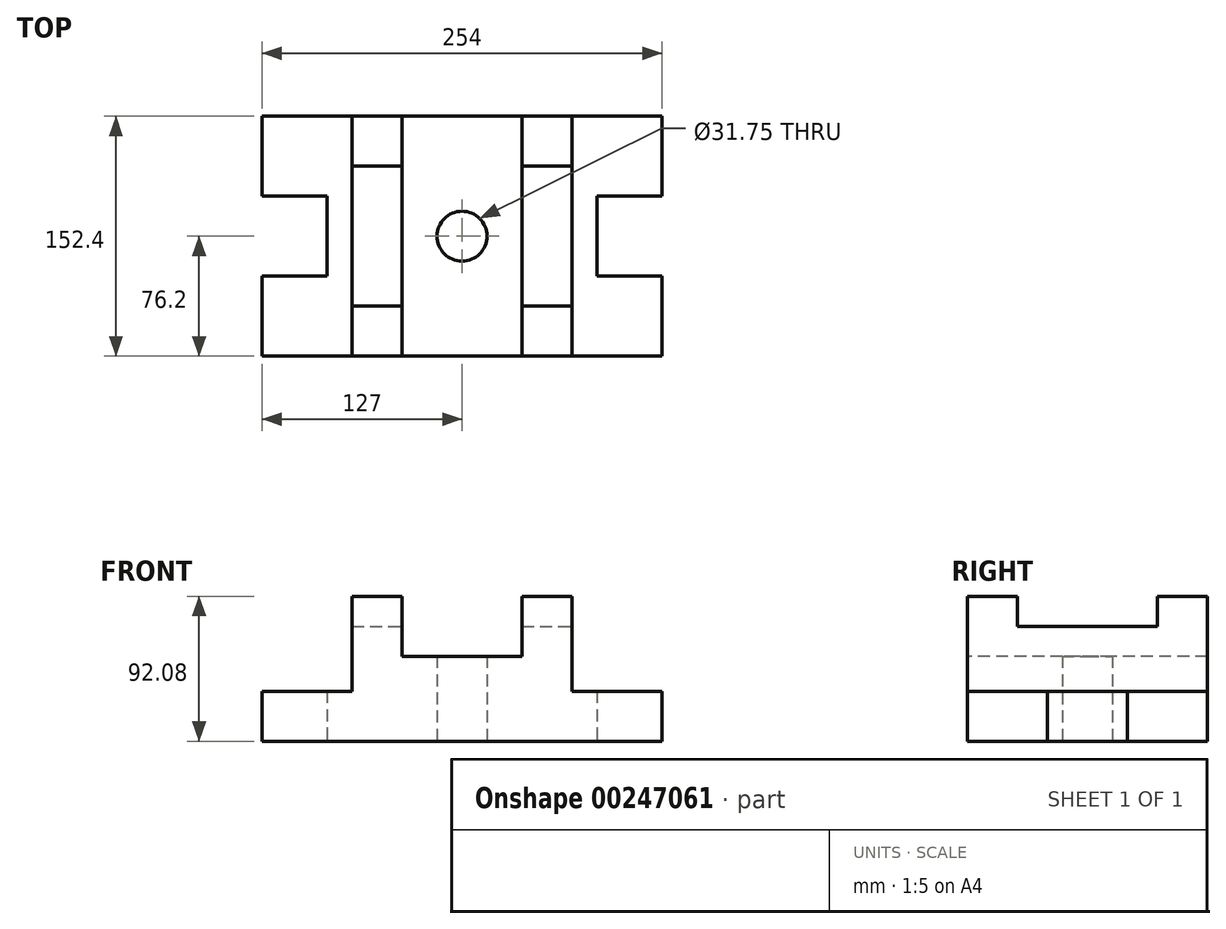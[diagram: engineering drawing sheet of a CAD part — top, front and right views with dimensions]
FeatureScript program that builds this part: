
annotation { "Feature Type Name" : "Feature", "Feature Type Description" : "" }
export const myFeature = defineFeature(function(context is Context, id is Id, definition is map)
    precondition{}
    {
        {
            var Q0;
            Q0=qCreatedBy(makeId("Top.planeOp"),FACE);
            var sketch = newSketch(context, id + "F0", { "sketchPlane" : qUnion([Q0])});
            skLineSegment(sketch, "E0.bottom", {"start": v(127, -76.2) * mm, "end": v(-127, -76.2) * mm});
            skLineSegment(sketch, "E0.top", {"start": v(127, 76.2) * mm, "end": v(-127, 76.2) * mm});
            skLineSegment(sketch, "E0.left", {"start": v(127, -76.2) * mm, "end": v(127, -25.4) * mm});
            skLineSegment(sketch, "E0.right", {"start": v(-127, -76.2) * mm, "end": v(-127, -25.4) * mm});
            skPoint(sketch, "E0.middle", {"position": v(0, 0) * mm});
            skLineSegment(sketch, "E1", {"start": v(38.1, 76.2) * mm, "end": v(38.1, -76.2) * mm});
            skLineSegment(sketch, "E2", {"start": v(-38.1, 76.2) * mm, "end": v(-38.1, -76.2) * mm});
            skLineSegment(sketch, "E3", {"start": v(69.85, 76.2) * mm, "end": v(69.85, -76.2) * mm});
            skLineSegment(sketch, "E4", {"start": v(-69.85, 76.2) * mm, "end": v(-69.85, -76.2) * mm});
            skLineSegment(sketch, "E5", {"start": v(-69.85, -44.45) * mm, "end": v(-38.1, -44.45) * mm});
            skLineSegment(sketch, "E6", {"start": v(-69.85, 44.45) * mm, "end": v(-38.1, 44.45) * mm});
            skLineSegment(sketch, "E7", {"start": v(38.1, 44.45) * mm, "end": v(69.85, 44.45) * mm});
            skLineSegment(sketch, "E8", {"start": v(38.1, -44.45) * mm, "end": v(69.85, -44.45) * mm});
            skLineSegment(sketch, "E9", {"start": v(-85.72, 25.4) * mm, "end": v(-85.72, -25.4) * mm});
            skLineSegment(sketch, "E10", {"start": v(85.72, 25.4) * mm, "end": v(85.72, -25.4) * mm});
            skLineSegment(sketch, "E11", {"start": v(85.72, -25.4) * mm, "end": v(127, -25.4) * mm});
            skLineSegment(sketch, "E12", {"start": v(85.72, 25.4) * mm, "end": v(127, 25.4) * mm});
            skLineSegment(sketch, "E13.trimOffspring", {"start": v(127, 25.4) * mm, "end": v(127, 76.2) * mm});
            skLineSegment(sketch, "E14", {"start": v(-127, 25.4) * mm, "end": v(-85.72, 25.4) * mm});
            skLineSegment(sketch, "E15", {"start": v(-127, -25.4) * mm, "end": v(-85.72, -25.4) * mm});
            skLineSegment(sketch, "E16.trimOffspring", {"start": v(-127, 25.4) * mm, "end": v(-127, 76.2) * mm});
            skCircle(sketch, "E17", {"center": v(0, 0) * mm, "radius": 15.88 * mm});
            skPoint(sketch, "E18.trimOffspring.end.orphan", {"position": v(0, -76.2) * mm});
            skPoint(sketch, "E19.start.orphan", {"position": v(0, 76.2) * mm});
            skSolve(sketch);
        }
        {
            var Q0;
            {var subQ0=sQuery(id+"F0.wireOp",EDGE,"E0.left");Q0=makeQuery(id+"F0.imprint","IMPRINT",FACE,{"disambiguationData":[TD([[makeQuery(id+"F0.imprint","IMPRINT",EDGE,{"derivedFrom":subQ0}),1.0]])]});}
            var Q1;
            {var subQ4=sQuery(id+"F0.wireOp",EDGE,"E12");Q1=makeQuery(id+"F0.imprint","IMPRINT",FACE,{"disambiguationData":[TD([[makeQuery(id+"F0.imprint","IMPRINT",EDGE,{"derivedFrom":subQ4}),1.0]])]});}
            var Q2;
            {var subQ4=sQuery(id+"F0.wireOp",EDGE,"E14");Q2=makeQuery(id+"F0.imprint","IMPRINT",FACE,{"disambiguationData":[TD([[makeQuery(id+"F0.imprint","IMPRINT",EDGE,{"derivedFrom":subQ4}),1.0]])]});}
            var Q3;
            {var subQ0=sQuery(id+"F0.wireOp",EDGE,"E0.right");Q3=makeQuery(id+"F0.imprint","IMPRINT",FACE,{"disambiguationData":[TD([[makeQuery(id+"F0.imprint","IMPRINT",EDGE,{"derivedFrom":subQ0}),-1.0]])]});}
            var Q4;
            {var subQ0=sQuery(id+"F0.wireOp",EDGE,"E4");var subQ7=sQuery(id+"F0.wireOp",EDGE,"E0.bottom");var subQ8=makeQuery(id+"F0.imprint","INTERSECT",VERTEX,{"derivedFrom":[subQ7,subQ0]});Q4=makeQuery(id+"F0.imprint","IMPRINT",FACE,{"disambiguationData":[TD([[makeQuery(id+"F0.imprint","IMPRINT",EDGE,{"disambiguationData":[TD([[subQ8,-1.0]])],"derivedFrom":subQ7}),-1.0]])]});}
            var Q5;
            {var subQ0=sQuery(id+"F0.wireOp",EDGE,"E3");var subQ9=sQuery(id+"F0.wireOp",EDGE,"E0.bottom");var subQ11=makeQuery(id+"F0.imprint","INTERSECT",VERTEX,{"derivedFrom":[subQ9,subQ0]});Q5=makeQuery(id+"F0.imprint","IMPRINT",FACE,{"disambiguationData":[TD([[makeQuery(id+"F0.imprint","IMPRINT",EDGE,{"disambiguationData":[TD([[subQ11,1.0]])],"derivedFrom":subQ9}),-1.0]])]});}
            extrude(context, id + "F1", {"entities" : qUnion([Q0, Q1, Q2, Q3, Q4, Q5]), "depth" : 31.75 * mm});
        }
        {
            var Q0;
            {var subQ0=sQuery(id+"F0.wireOp",EDGE,"E5");Q0=makeQuery(id+"F0.imprint","IMPRINT",FACE,{"disambiguationData":[TD([[makeQuery(id+"F0.imprint","IMPRINT",EDGE,{"derivedFrom":subQ0}),1.0]])]});}
            var Q1;
            {var subQ0=sQuery(id+"F0.wireOp",EDGE,"E7");Q1=makeQuery(id+"F0.imprint","IMPRINT",FACE,{"disambiguationData":[TD([[makeQuery(id+"F0.imprint","IMPRINT",EDGE,{"derivedFrom":subQ0}),-1.0]])]});}
            extrude(context, id + "F2", {"entities" : qUnion([Q0, Q1]), "operationType" : NewBodyOperationType.ADD, "depth" : 73.02 * mm});
        }
        {
            var Q0;
            {var subQ5=sQuery(id+"F0.wireOp",EDGE,"E8");Q0=makeQuery(id+"F0.imprint","IMPRINT",FACE,{"disambiguationData":[TD([[makeQuery(id+"F0.imprint","IMPRINT",EDGE,{"derivedFrom":subQ5}),-1.0]])]});}
            var Q1;
            {var subQ5=sQuery(id+"F0.wireOp",EDGE,"E5");Q1=makeQuery(id+"F0.imprint","IMPRINT",FACE,{"disambiguationData":[TD([[makeQuery(id+"F0.imprint","IMPRINT",EDGE,{"derivedFrom":subQ5}),-1.0]])]});}
            var Q2;
            {var subQ5=sQuery(id+"F0.wireOp",EDGE,"E6");Q2=makeQuery(id+"F0.imprint","IMPRINT",FACE,{"disambiguationData":[TD([[makeQuery(id+"F0.imprint","IMPRINT",EDGE,{"derivedFrom":subQ5}),1.0]])]});}
            var Q3;
            {var subQ5=sQuery(id+"F0.wireOp",EDGE,"E7");Q3=makeQuery(id+"F0.imprint","IMPRINT",FACE,{"disambiguationData":[TD([[makeQuery(id+"F0.imprint","IMPRINT",EDGE,{"derivedFrom":subQ5}),1.0]])]});}
            extrude(context, id + "F3", {"entities" : qUnion([Q0, Q1, Q2, Q3]), "operationType" : NewBodyOperationType.ADD, "depth" : 92.07 * mm});
        }
        {
            var Q0;
            Q0=makeQuery(id+"F0.imprint","IMPRINT",FACE,{"disambiguationData":[TD([[makeQuery(id+"F0.imprint","IMPRINT",EDGE,{"derivedFrom":sQuery(id+"F0.wireOp",EDGE,"E17")}),-1.0]])]});
            extrude(context, id + "F4", {"entities" : qUnion([Q0]), "operationType" : NewBodyOperationType.ADD, "depth" : 53.97 * mm});
        }
    });
